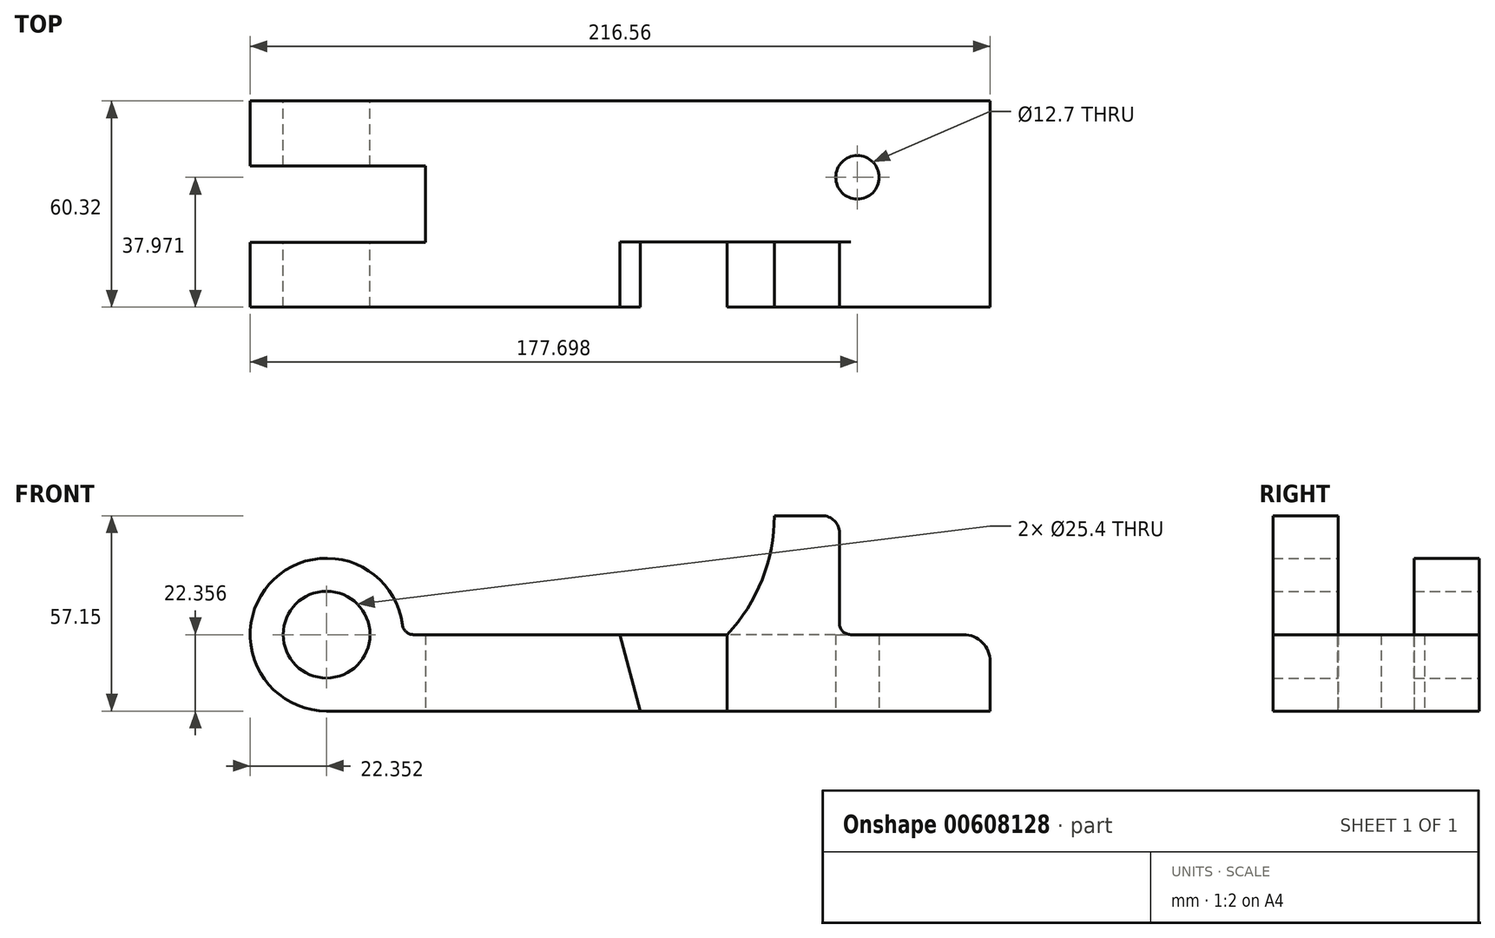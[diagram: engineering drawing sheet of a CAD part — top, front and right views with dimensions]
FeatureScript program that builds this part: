
annotation { "Feature Type Name" : "Feature", "Feature Type Description" : "" }
export const myFeature = defineFeature(function(context is Context, id is Id, definition is map)
    precondition{}
    {
        {
            var Q0;
            Q0=qCreatedBy(makeId("Front.planeOp"),FACE);
            var sketch = newSketch(context, id + "F0", { "sketchPlane" : qUnion([Q0])});
            skLineSegment(sketch, "E0.bottom", {"start": v(108.28, -11.18) * mm, "end": v(-85.93, -11.18) * mm});
            skLineSegment(sketch, "E0.top", {"start": v(108.28, 11.18) * mm, "end": v(-63.58, 11.18) * mm});
            skLineSegment(sketch, "E0.left", {"start": v(108.28, -11.18) * mm, "end": v(108.28, 11.18) * mm});
            skPoint(sketch, "E0.middle", {"position": v(0, 0) * mm});
            skArc(sketch, "E1", {"start": v(-63.58, 11.18) * mm, "mid": v(-101.73, 26.98) * mm, "end": v(-85.93, -11.18) * mm});
            skCircle(sketch, "E2", {"center": v(-85.93, 11.18) * mm, "radius": 12.7 * mm});
            skLineSegment(sketch, "E3", {"start": v(-85.93, 11.18) * mm, "end": v(-85.93, 0) * mm, "construction": true});
            skLineSegment(sketch, "E4", {"start": v(-85.93, 0) * mm, "end": v(0, 0) * mm, "construction": true});
            skSolve(sketch);
        }
        {
            var Q0;
            Q0=makeQuery(id+"F0.imprint","IMPRINT",FACE,{"disambiguationData":[TD([[makeQuery(id+"F0.imprint","IMPRINT",EDGE,{"derivedFrom":sQuery(id+"F0.wireOp",EDGE,"E0.bottom")}),-1.0]])]});
            extrude(context, id + "F1", {"entities" : qUnion([Q0]), "endBound" : BoundingType.SYMMETRIC, "depth" : 60.32 * mm, "offsetDistance" : 25.4 * mm});
        }
        {
            var Q0;
            Q0=makeQuery(id+"F1.opExtrude","SWEPT_FACE",FACE,{"disambiguationData":[OSD([sQuery(id+"F0.wireOp",EDGE,"E0.bottom")])]});
            var sketch = newSketch(context, id + "F2", { "sketchPlane" : qUnion([Q0])});
            skLineSegment(sketch, "E5.bottom", {"start": v(-56.97, -11.16) * mm, "end": v(-114.88, -11.16) * mm});
            skLineSegment(sketch, "E5.top", {"start": v(-56.97, 11.16) * mm, "end": v(-114.88, 11.16) * mm});
            skLineSegment(sketch, "E5.left", {"start": v(-56.97, -11.16) * mm, "end": v(-56.97, 11.16) * mm});
            skLineSegment(sketch, "E5.right", {"start": v(-114.88, -11.16) * mm, "end": v(-114.88, 11.16) * mm});
            skPoint(sketch, "E5.middle", {"position": v(-85.93, 0) * mm});
            skCircle(sketch, "E6", {"center": v(69.42, -7.81) * mm, "radius": 6.35 * mm});
            skSolve(sketch);
        }
        {
            var Q0;
            {var subQ0=sQuery(id+"F2.wireOp",EDGE,"E5.right");Q0=makeQuery(id+"F2.imprint","IMPRINT",FACE,{"disambiguationData":[TD([[makeQuery(id+"F2.imprint","IMPRINT",EDGE,{"derivedFrom":subQ0}),-1.0]])]});}
            var Q1;
            Q1=makeQuery(id+"F2.imprint","IMPRINT",FACE,{"disambiguationData":[TD([[makeQuery(id+"F2.imprint","IMPRINT",EDGE,{"derivedFrom":sQuery(id+"F2.wireOp",EDGE,"E6")}),1.0]])]});
            var Q2;
            {var subQ0=sQuery(id+"F2.wireOp",EDGE,"E5.left");Q2=makeQuery(id+"F2.imprint","IMPRINT",FACE,{"disambiguationData":[TD([[makeQuery(id+"F2.imprint","IMPRINT",EDGE,{"derivedFrom":subQ0}),1.0]])]});}
            extrude(context, id + "F3", {"entities" : qUnion([Q0, Q1, Q2]), "operationType" : NewBodyOperationType.REMOVE, "endBound" : BoundingType.THROUGH_ALL, "oppositeDirection" : true, "depth" : 25.4 * mm, "offsetDistance" : 25.4 * mm});
        }
        {
            var Q0;
            Q0=makeQuery(id+"F1.opExtrude","CAP_FACE",FACE,{"disambiguationData":[OSD([sQuery(id+"F0.wireOp",EDGE,"E0.bottom"),sQuery(id+"F0.wireOp",EDGE,"E0.top"),sQuery(id+"F0.wireOp",EDGE,"E0.left"),sQuery(id+"F0.wireOp",EDGE,"E1"),sQuery(id+"F0.wireOp",EDGE,"E2")])],"isStart":false});
            var sketch = newSketch(context, id + "F4", { "sketchPlane" : qUnion([Q0])});
            skLineSegment(sketch, "E7", {"start": v(31.32, 11.18) * mm, "end": v(31.32, -11.18) * mm});
            skLineSegment(sketch, "E8", {"start": v(31.32, -11.18) * mm, "end": v(5.92, -11.18) * mm});
            skLineSegment(sketch, "E9", {"start": v(5.92, -11.18) * mm, "end": v(-0.08, 11.18) * mm});
            skLineSegment(sketch, "E10", {"start": v(-0.08, 11.18) * mm, "end": v(31.32, 11.18) * mm});
            skSolve(sketch);
        }
        {
            var Q0;
            Q0=makeQuery(id+"F4.imprint","IMPRINT",FACE,{"disambiguationData":[TD([[makeQuery(id+"F4.imprint","IMPRINT",EDGE,{"derivedFrom":sQuery(id+"F4.wireOp",EDGE,"E7")}),-1.0]])]});
            extrude(context, id + "F5", {"entities" : qUnion([Q0]), "operationType" : NewBodyOperationType.REMOVE, "oppositeDirection" : true, "depth" : 19.05 * mm, "offsetDistance" : 25.4 * mm});
        }
        {
            var Q0;
            {var subQ0=sQuery(id+"F0.wireOp",EDGE,"E0.bottom");var subQ1=sQuery(id+"F0.wireOp",EDGE,"E0.top");var subQ2=sQuery(id+"F0.wireOp",EDGE,"E0.left");Q0=makeQuery(id+"F5.boolean.opBoolean","SPLIT",FACE,{"disambiguationData":[TD([makeQuery(id+"F1.opExtrude","SWEPT_FACE",FACE,{"disambiguationData":[OSD([subQ2])]})])],"derivedFrom":makeQuery(id+"F1.opExtrude","CAP_FACE",FACE,{"disambiguationData":[OSD([subQ0,subQ1,subQ2,sQuery(id+"F0.wireOp",EDGE,"E1"),sQuery(id+"F0.wireOp",EDGE,"E2")])],"isStart":false})});}
            var sketch = newSketch(context, id + "F6", { "sketchPlane" : qUnion([Q0])});
            skLineSegment(sketch, "E11.bottom", {"start": v(45.11, 9.14) * mm, "end": v(64.16, 9.14) * mm});
            skLineSegment(sketch, "E11.top", {"start": v(45.11, 45.97) * mm, "end": v(64.16, 45.97) * mm});
            skLineSegment(sketch, "E11.right", {"start": v(64.16, 9.14) * mm, "end": v(64.16, 45.97) * mm});
            skPoint(sketch, "E11.middle", {"position": v(54.64, 27.56) * mm});
            skArc(sketch, "E12", {"start": v(31.32, 11.18) * mm, "mid": v(41.54, 27.26) * mm, "end": v(45.11, 45.97) * mm});
            skPoint(sketch, "E12.second.point", {"position": v(31.32, 11.18) * mm});
            skPoint(sketch, "E12.third.point", {"position": v(-49.1, 72.36) * mm});
            skLineSegment(sketch, "E13", {"start": v(45.11, 9.14) * mm, "end": v(31.32, 9.14) * mm});
            skLineSegment(sketch, "E14", {"start": v(31.32, 9.14) * mm, "end": v(31.32, 11.18) * mm});
            skSolve(sketch);
        }
        {
            var Q0;
            {var subQ0=sQuery(id+"F6.wireOp",EDGE,"E11.top");Q0=makeQuery(id+"F6.imprint","IMPRINT",FACE,{"disambiguationData":[TD([[makeQuery(id+"F6.imprint","IMPRINT",EDGE,{"derivedFrom":subQ0}),-1.0]])]});}
            var Q1;
            {var subQ0=sQuery(id+"F6.wireOp",EDGE,"E11.bottom");Q1=makeQuery(id+"F6.imprint","IMPRINT",FACE,{"disambiguationData":[TD([[makeQuery(id+"F6.imprint","IMPRINT",EDGE,{"derivedFrom":subQ0}),1.0]])]});}
            extrude(context, id + "F7", {"entities" : qUnion([Q0, Q1]), "operationType" : NewBodyOperationType.ADD, "oppositeDirection" : true, "depth" : 19.05 * mm, "offsetDistance" : 25.4 * mm});
        }
        {
            var Q0;
            {var subQ0=sQuery(id+"F0.wireOp",EDGE,"E1");var subQ1=sQuery(id+"F0.wireOp",EDGE,"E0.top");Q0=makeQuery(id+"F3.boolean.opBoolean","SPLIT",EDGE,{"disambiguationData":[TD([makeQuery(id+"F3.opExtrude","SWEPT_FACE",FACE,{"disambiguationData":[OSD([sQuery(id+"F2.wireOp",EDGE,"E5.bottom")])]})])],"derivedFrom":makeQuery(id+"F1.opExtrude","SWEPT_EDGE",EDGE,{"disambiguationData":[OSD([subQ1,subQ0])]})});}
            var Q1;
            {var subQ0=sQuery(id+"F0.wireOp",EDGE,"E1");var subQ1=sQuery(id+"F0.wireOp",EDGE,"E0.top");Q1=makeQuery(id+"F3.boolean.opBoolean","SPLIT",EDGE,{"disambiguationData":[TD([makeQuery(id+"F3.opExtrude","SWEPT_FACE",FACE,{"disambiguationData":[OSD([sQuery(id+"F2.wireOp",EDGE,"E5.top")])]})])],"derivedFrom":makeQuery(id+"F1.opExtrude","SWEPT_EDGE",EDGE,{"disambiguationData":[OSD([subQ1,subQ0])]})});}
            fillet(context, id + "F8", {"entities" : qUnion([Q0, Q1]), "radius" : 3.3 * mm, "tangentPropagation" : true, "allowEdgeOverflow" : false});
        }
        {
            var Q0;
            Q0=makeQuery(id+"F1.opExtrude","SWEPT_EDGE",EDGE,{"disambiguationData":[OSD([sQuery(id+"F0.wireOp",EDGE,"E0.top"),sQuery(id+"F0.wireOp",EDGE,"E0.left")])]});
            fillet(context, id + "F9", {"entities" : qUnion([Q0]), "radius" : 7.87 * mm, "tangentPropagation" : true, "allowEdgeOverflow" : false});
        }
        {
            var Q0;
            Q0=makeQuery(id+"F7.boolean.opBoolean","INTERSECT",EDGE,{"derivedFrom":[makeQuery(id+"F1.opExtrude","SWEPT_FACE",FACE,{"disambiguationData":[OSD([sQuery(id+"F0.wireOp",EDGE,"E0.top")])]}),makeQuery(id+"F7.opExtrude","SWEPT_FACE",FACE,{"disambiguationData":[OSD([sQuery(id+"F6.wireOp",EDGE,"E11.right")])]})]});
            fillet(context, id + "F10", {"entities" : qUnion([Q0]), "radius" : 3.3 * mm, "tangentPropagation" : true, "allowEdgeOverflow" : false});
        }
        {
            var Q0;
            Q0=makeQuery(id+"F7.opExtrude","SWEPT_EDGE",EDGE,{"disambiguationData":[OSD([sQuery(id+"F6.wireOp",EDGE,"E11.top"),sQuery(id+"F6.wireOp",EDGE,"E11.right")])]});
            fillet(context, id + "F11", {"entities" : qUnion([Q0]), "radius" : 5.08 * mm, "tangentPropagation" : true, "allowEdgeOverflow" : false});
        }
    });
